# Revit family: QF_COMENDA_B02060_B02460CAT
name_source: partatom
category: Attrezzature speciali
units: mm (PartAtom-declared; Revit-internal decimal feet)

## family parameters
Basato su piano di lavoro = No
Condiviso = No
Numero OmniClass = 23.40.40.14
Punto di calcolo locali = No
Quota connettore circolare = Usa diametro
Sempre verticale = Sì
Taglio con vuoti quando caricato = No
Tipo di parte = Normale
Titolo OmniClass = Food Service Equipment

## types (2) — shared parameters
Altezza = 630 mm  [stored 2.06693 ft]
Altezza allacciamento acqua fredda da pavimento finito = 76 mm  [stored 0.249344 ft]
Altezza allacciamento elettrico da pavimento finito = 76 mm  [stored 0.249344 ft]
Altezza dello scarico diretto acqua da pavimento finito = 35 mm  [stored 0.114829 ft]
Corrente di funzionamento normale = 12 A
Diametro condotta acqua fredda = 1"
Diametro dello scarico diretto di acqua = 1 1/2"
Fase = 1
Frequenza = 50 Hz
Lunghezza = 460 mm  [stored 1.50919 ft]
Modello = EB28
Numero dei poli = 1
Peso netto = 40.00 kg
Pessione minima acqua fredda = 2000.0 Pa
Potenza elettrica = 2760 W
Produttore = COMENDA
Profondità = 515 mm  [stored 1.68963 ft]
Protezione contro le sovracorrenti = 16 A
Temperatura raccomandata per acqua fredda = 15 °C
Tensione = 230 V
URL = www.comenda.eu
URL catalogo = https://comenda.eu
zero-valued in all types: Prospetto di default

## per-type parameters (varying)
| type | Descrizione |
| B02060 | SINGLE-PHASE GLASSWASHER |
| B02460 | SINGLE-PHASE GLASSWASHER WITH WATER SOFTENER |

note: [stored X ft] marks values corroborated as IEEE doubles in the binary element streams (Revit-internal decimal feet)

## geometry (parser evidence)
native form markers: Sweep x3
no freeform markers — native parametric forms only
